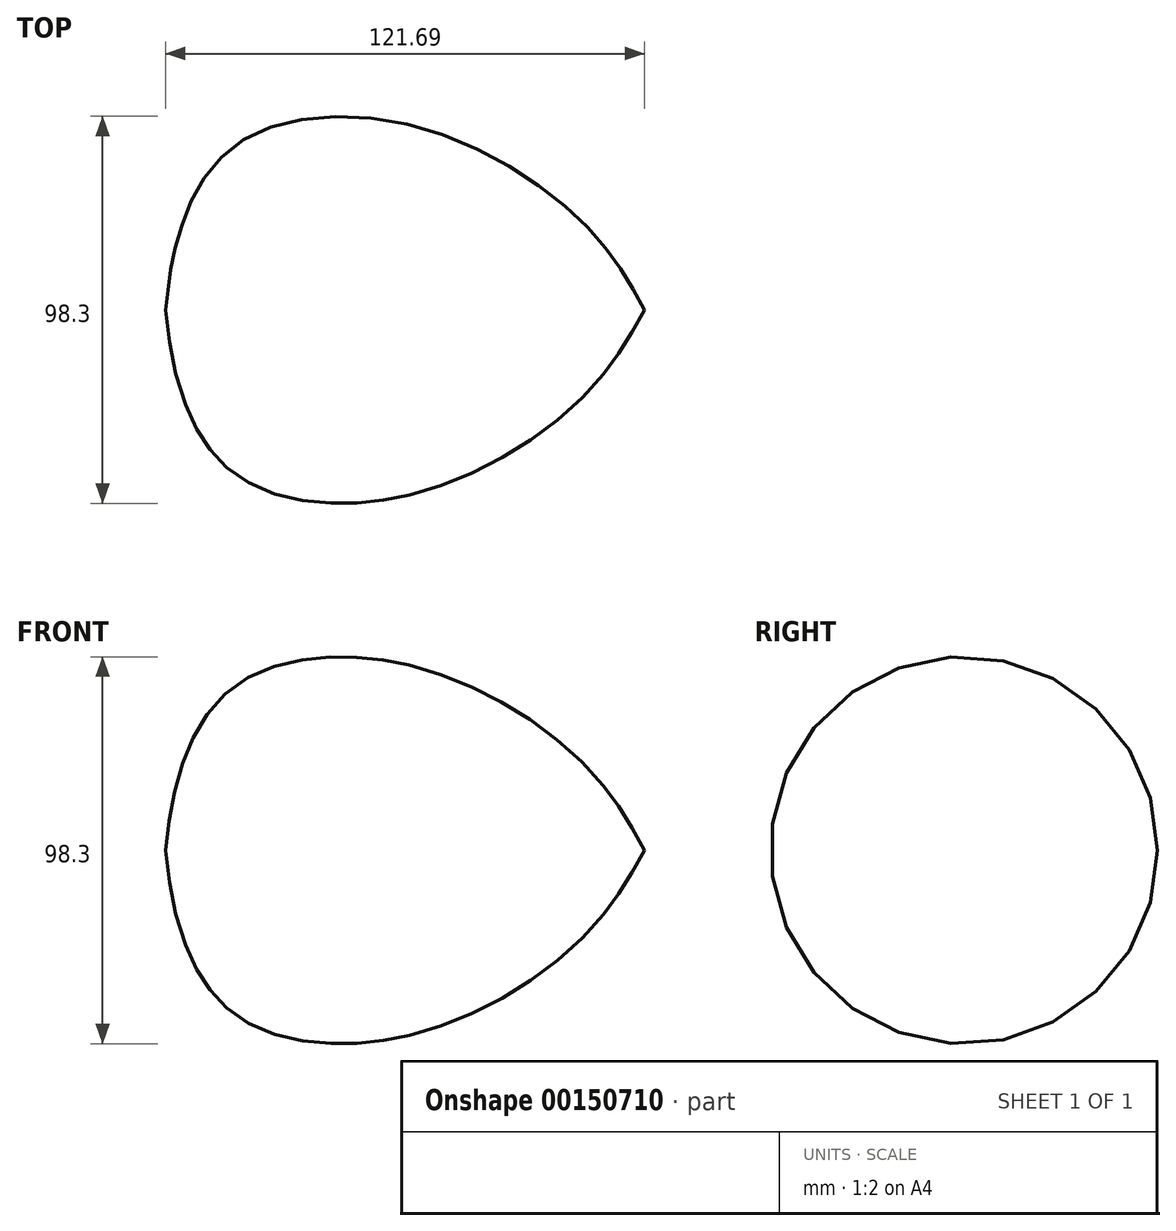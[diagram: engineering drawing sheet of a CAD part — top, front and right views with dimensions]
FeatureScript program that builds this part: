
annotation { "Feature Type Name" : "Feature", "Feature Type Description" : "" }
export const myFeature = defineFeature(function(context is Context, id is Id, definition is map)
    precondition{}
    {
        {
            var Q0;
            Q0=qCreatedBy(makeId("Top.planeOp"),FACE);
            var sketch = newSketch(context, id + "F0", { "sketchPlane" : qUnion([Q0])});
            skFitSpline(sketch, "E0", {"points": [v(-54.6, 0) * mm, v(-51.4, 18.44) * mm, v(-36.3, 42.26) * mm, v(7.84, 46.9) * mm, v(51.7, 21.93) * mm, v(67.09, 0) * mm], "startDerivative": vector(12.65, 115.8) * mm, "endDerivative": vector(66.59, -120.2) * mm});
            skSolve(sketch);
        }
        {
            var Q0;
            Q0=qCreatedBy(makeId("Top.planeOp"),FACE);
            var sketch = newSketch(context, id + "F1", { "sketchPlane" : qUnion([Q0])});
            skLineSegment(sketch, "E1", {"start": v(-54.89, 0) * mm, "end": v(67.38, 0) * mm});
            skSolve(sketch);
        }
        {
            var Q0;
            Q0=sQuery(id+"F0.wireOp",EDGE,"E0");
            var Q1;
            Q1=sQuery(id+"F1.wireOp",EDGE,"E1");
            revolve(context, id + "F2", {"bodyType" : ToolBodyType.SURFACE, "surfaceEntities" : qUnion([Q0]), "axis" : qUnion([Q1]), "revolveType" : RevolveType.FULL});
        }
    });
